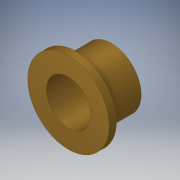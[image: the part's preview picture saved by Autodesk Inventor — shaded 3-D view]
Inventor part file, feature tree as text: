
AUTODESK INVENTOR PART (.ipt)
format: ipt  version: 2019.4 (Build 234330000, 330)  size: 114,688 bytes
history: native  units: in
note: dims shown in document units (in); Inventor stores cm internally (conversion verified against a paired STEP export)
features: extrude x2, sketch x2, projected_geometry x1
ambient origin geometry x8: Origin, YZ Plane, XZ Plane, XY Plane, X Axis, Y Axis, Z Axis, Center Point
bodies: Solid1 (feature_tree)
feature tree (5):
  extrude  "Extrusion1"  Depth=0.375in
  extrude  "Extrusion2"  Depth=0.0625in
  sketch  "Sketch1"  dims[d0=0.501in d1=0.375in]
  sketch  "Sketch2"  dims[d2=0.365in d3=0.0in d4=0.688in d5=0.0625in d6=0.0in]
  projected_geometry  "Projected Loop1"
